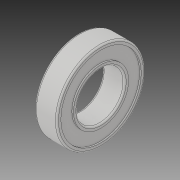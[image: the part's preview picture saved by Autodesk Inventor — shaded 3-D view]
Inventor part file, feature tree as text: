
AUTODESK INVENTOR PART (.ipt)
format: ipt  version: 2019 (Build 230136000, 136)  size: 146,944 bytes
history: native  units: in
note: dims shown in document units (in); Inventor stores cm internally (conversion verified against a paired STEP export)
features: fillet x1
ambient origin geometry x8: Origin, YZ Plane, XZ Plane, XY Plane, X Axis, Y Axis, Z Axis, Center Point
bodies: Solid1 (feature_tree)
feature tree (1):
  fillet  "Fillet1"  [1 undecoded]
note: 1 required parameter value undecoded (feature->parameter linkage not recoverable at this tier; creation-order binding heuristic only, values carry confidence <= 0.55)
